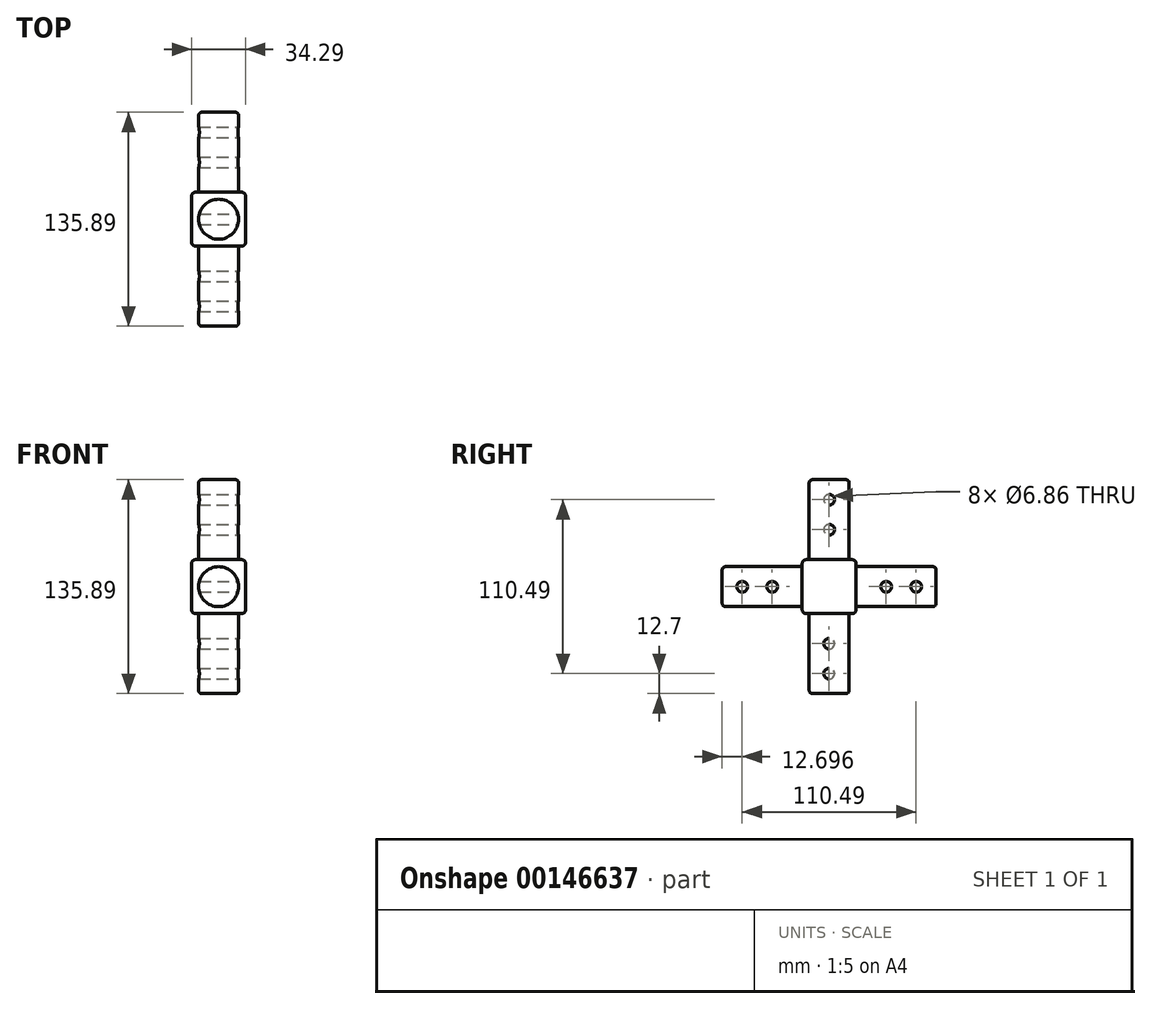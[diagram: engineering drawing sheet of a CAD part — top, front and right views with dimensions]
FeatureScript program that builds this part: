
annotation { "Feature Type Name" : "Feature", "Feature Type Description" : "" }
export const myFeature = defineFeature(function(context is Context, id is Id, definition is map)
    precondition{}
    {
        {
            var Q0;
            Q0=qCreatedBy(makeId("Top.planeOp"),FACE);
            var sketch = newSketch(context, id + "F0", { "sketchPlane" : qUnion([Q0])});
            skLineSegment(sketch, "E0.bottom", {"start": v(-13.47, 23.7) * mm, "end": v(20.82, 23.7) * mm});
            skLineSegment(sketch, "E0.top", {"start": v(-13.47, -10.58) * mm, "end": v(20.82, -10.58) * mm});
            skLineSegment(sketch, "E0.left", {"start": v(-13.47, 23.7) * mm, "end": v(-13.47, -10.58) * mm});
            skLineSegment(sketch, "E0.right", {"start": v(20.82, 23.7) * mm, "end": v(20.82, -10.58) * mm});
            skSolve(sketch);
        }
        {
            var Q0;
            Q0=qSketchRegion(id+"F0",true);
            extrude(context, id + "F1", {"entities" : qUnion([Q0]), "depth" : 34.3 * mm});
        }
        {
            var Q0;
            Q0=makeQuery(id+"F1.opExtrude","CAP_FACE",FACE,{"disambiguationData":[OSD([sQuery(id+"F0.wireOp",EDGE,"E0.bottom"),sQuery(id+"F0.wireOp",EDGE,"E0.top"),sQuery(id+"F0.wireOp",EDGE,"E0.left"),sQuery(id+"F0.wireOp",EDGE,"E0.right")])],"isStart":false});
            var sketch = newSketch(context, id + "F2", { "sketchPlane" : qUnion([Q0])});
            skCircle(sketch, "E1", {"center": v(3.68, 6.56) * mm, "radius": 12.7 * mm});
            skLineSegment(sketch, "E2", {"start": v(3.67, 23.7) * mm, "end": v(3.67, -12.79) * mm, "construction": true});
            skLineSegment(sketch, "E3", {"start": v(20.82, 6.56) * mm, "end": v(-13.47, 6.56) * mm, "construction": true});
            skSolve(sketch);
        }
        {
            var Q0;
            Q0=qSketchRegion(id+"F2",true);
            extrude(context, id + "F3", {"entities" : qUnion([Q0]), "operationType" : NewBodyOperationType.ADD, "depth" : 50.8 * mm});
        }
        {
            var Q0;
            Q0=makeQuery(id+"F1.opExtrude","SWEPT_FACE",FACE,{"disambiguationData":[OSD([sQuery(id+"F0.wireOp",EDGE,"E0.top")])]});
            var sketch = newSketch(context, id + "F4", { "sketchPlane" : qUnion([Q0])});
            skLineSegment(sketch, "E4", {"start": v(-13.47, 17.15) * mm, "end": v(24.43, 17.15) * mm, "construction": true});
            skLineSegment(sketch, "E5", {"start": v(3.67, 0) * mm, "end": v(3.67, 34.3) * mm, "construction": true});
            skCircle(sketch, "E6", {"center": v(3.67, 17.15) * mm, "radius": 12.7 * mm});
            skSolve(sketch);
        }
        {
            var Q0;
            Q0=qSketchRegion(id+"F4",true);
            extrude(context, id + "F5", {"entities" : qUnion([Q0]), "operationType" : NewBodyOperationType.ADD, "depth" : 50.8 * mm});
        }
        {
            var Q0;
            Q0=qCreatedBy(makeId("Right.planeOp"),FACE);
            var sketch = newSketch(context, id + "F6", { "sketchPlane" : qUnion([Q0])});
            skCircle(sketch, "E7", {"center": v(6.56, 53.34) * mm, "radius": 3.43 * mm});
            skCircle(sketch, "E8", {"center": v(6.56, 72.4) * mm, "radius": 3.43 * mm});
            skSolve(sketch);
        }
        {
            var Q0;
            Q0=qSketchRegion(id+"F6",true);
            extrude(context, id + "F7", {"entities" : qUnion([Q0]), "operationType" : NewBodyOperationType.REMOVE, "endBound" : BoundingType.SYMMETRIC, "oppositeDirection" : true, "depth" : 50.8 * mm});
        }
        {
            var Q0;
            Q0=qCreatedBy(makeId("Right.planeOp"),FACE);
            var sketch = newSketch(context, id + "F8", { "sketchPlane" : qUnion([Q0])});
            skCircle(sketch, "E9", {"center": v(-29.63, 17.15) * mm, "radius": 3.43 * mm});
            skCircle(sketch, "E10", {"center": v(-48.68, 17.15) * mm, "radius": 3.43 * mm});
            skSolve(sketch);
        }
        {
            var Q0;
            Q0=qSketchRegion(id+"F8",true);
            extrude(context, id + "F9", {"entities" : qUnion([Q0]), "operationType" : NewBodyOperationType.REMOVE, "endBound" : BoundingType.SYMMETRIC, "oppositeDirection" : true, "depth" : 50.8 * mm});
        }
        {
            var Q0;
            Q0=qCreatedBy(makeId("Front.planeOp"),FACE);
            var sketch = newSketch(context, id + "F10", { "sketchPlane" : qUnion([Q0])});
            skCircle(sketch, "E11", {"center": v(-51.57, 17.15) * mm, "radius": 3.43 * mm});
            skCircle(sketch, "E12", {"center": v(-32.52, 17.15) * mm, "radius": 3.43 * mm});
            skSolve(sketch);
        }
        {
            var Q0;
            Q0=qSketchRegion(id+"F10",true);
            extrude(context, id + "F11", {"entities" : qUnion([Q0]), "operationType" : NewBodyOperationType.REMOVE, "endBound" : BoundingType.SYMMETRIC, "oppositeDirection" : true, "depth" : 50.8 * mm});
        }
        {
            var Q0;
            Q0=makeQuery(id+"F1.opExtrude","SWEPT_EDGE",EDGE,{"disambiguationData":[OSD([sQuery(id+"F0.wireOp",EDGE,"E0.bottom"),sQuery(id+"F0.wireOp",EDGE,"E0.right")])]});
            var Q1;
            Q1=makeQuery(id+"F1.opExtrude","CAP_EDGE",EDGE,{"disambiguationData":[OSD([sQuery(id+"F0.wireOp",EDGE,"E0.right")])],"isStart":false});
            var Q2;
            Q2=makeQuery(id+"F1.opExtrude","SWEPT_EDGE",EDGE,{"disambiguationData":[OSD([sQuery(id+"F0.wireOp",EDGE,"E0.top"),sQuery(id+"F0.wireOp",EDGE,"E0.right")])]});
            var Q3;
            Q3=makeQuery(id+"F1.opExtrude","CAP_EDGE",EDGE,{"disambiguationData":[OSD([sQuery(id+"F0.wireOp",EDGE,"E0.right")])],"isStart":true});
            var Q4;
            Q4=makeQuery(id+"F1.opExtrude","CAP_EDGE",EDGE,{"disambiguationData":[OSD([sQuery(id+"F0.wireOp",EDGE,"E0.bottom")])],"isStart":true});
            var Q5;
            Q5=makeQuery(id+"F1.opExtrude","CAP_EDGE",EDGE,{"disambiguationData":[OSD([sQuery(id+"F0.wireOp",EDGE,"E0.bottom")])],"isStart":false});
            var Q6;
            Q6=makeQuery(id+"F1.opExtrude","SWEPT_EDGE",EDGE,{"disambiguationData":[OSD([sQuery(id+"F0.wireOp",EDGE,"E0.bottom"),sQuery(id+"F0.wireOp",EDGE,"E0.left")])]});
            var Q7;
            Q7=makeQuery(id+"F1.opExtrude","CAP_EDGE",EDGE,{"disambiguationData":[OSD([sQuery(id+"F0.wireOp",EDGE,"E0.left")])],"isStart":true});
            var Q8;
            Q8=makeQuery(id+"F1.opExtrude","CAP_EDGE",EDGE,{"disambiguationData":[OSD([sQuery(id+"F0.wireOp",EDGE,"E0.top")])],"isStart":true});
            var Q9;
            Q9=makeQuery(id+"F1.opExtrude","CAP_EDGE",EDGE,{"disambiguationData":[OSD([sQuery(id+"F0.wireOp",EDGE,"E0.left")])],"isStart":false});
            var Q10;
            Q10=makeQuery(id+"F1.opExtrude","SWEPT_EDGE",EDGE,{"disambiguationData":[OSD([sQuery(id+"F0.wireOp",EDGE,"E0.top"),sQuery(id+"F0.wireOp",EDGE,"E0.left")])]});
            var Q11;
            Q11=makeQuery(id+"F1.opExtrude","CAP_EDGE",EDGE,{"disambiguationData":[OSD([sQuery(id+"F0.wireOp",EDGE,"E0.top")])],"isStart":false});
            fillet(context, id + "F12", {"entities" : qUnion([Q0, Q1, Q2, Q3, Q4, Q5, Q6, Q7, Q8, Q9, Q10, Q11]), "radius" : 2.54 * mm, "tangentPropagation" : true, "allowEdgeOverflow" : false});
        }
        {
            var Q0;
            Q0=makeQuery(id+"F1.opExtrude","SWEPT_FACE",FACE,{"disambiguationData":[OSD([sQuery(id+"F0.wireOp",EDGE,"E0.bottom")])]});
            var sketch = newSketch(context, id + "F13", { "sketchPlane" : qUnion([Q0])});
            skLineSegment(sketch, "E13", {"start": v(-18.28, 17.15) * mm, "end": v(4.82, 17.15) * mm, "construction": true});
            skPoint(sketch, "E13.endSnap0", {"position": v(-18.28, 17.15) * mm});
            skLineSegment(sketch, "E14", {"start": v(-3.67, 31.75) * mm, "end": v(-3.67, 14.65) * mm, "construction": true});
            skCircle(sketch, "E15", {"center": v(-3.67, 17.15) * mm, "radius": 12.7 * mm});
            skSolve(sketch);
        }
        {
            var Q0;
            Q0=qSketchRegion(id+"F13",true);
            extrude(context, id + "F14", {"entities" : qUnion([Q0]), "operationType" : NewBodyOperationType.ADD, "depth" : 50.8 * mm});
        }
        {
            var Q0;
            Q0=qCreatedBy(makeId("Right.planeOp"),FACE);
            var sketch = newSketch(context, id + "F15", { "sketchPlane" : qUnion([Q0])});
            skCircle(sketch, "E16", {"center": v(42.76, 17.15) * mm, "radius": 3.43 * mm});
            skCircle(sketch, "E17", {"center": v(61.8, 17.15) * mm, "radius": 3.43 * mm});
            skSolve(sketch);
        }
        {
            var Q0;
            Q0=qSketchRegion(id+"F15",true);
            extrude(context, id + "F16", {"entities" : qUnion([Q0]), "operationType" : NewBodyOperationType.REMOVE, "endBound" : BoundingType.SYMMETRIC, "oppositeDirection" : true, "depth" : 50.8 * mm});
        }
        {
            var Q0;
            Q0=qCreatedBy(makeId("Front.planeOp"),FACE);
            var sketch = newSketch(context, id + "F17", { "sketchPlane" : qUnion([Q0])});
            skCircle(sketch, "E18", {"center": v(58.92, 17.15) * mm, "radius": 3.43 * mm});
            skCircle(sketch, "E19", {"center": v(39.87, 17.15) * mm, "radius": 3.43 * mm});
            skSolve(sketch);
        }
        {
            var Q0;
            Q0=qSketchRegion(id+"F17",true);
            extrude(context, id + "F18", {"entities" : qUnion([Q0]), "operationType" : NewBodyOperationType.REMOVE, "endBound" : BoundingType.SYMMETRIC, "oppositeDirection" : true, "depth" : 50.8 * mm});
        }
        {
            var Q0;
            Q0=makeQuery(id+"F1.opExtrude","CAP_FACE",FACE,{"disambiguationData":[OSD([sQuery(id+"F0.wireOp",EDGE,"E0.bottom"),sQuery(id+"F0.wireOp",EDGE,"E0.top"),sQuery(id+"F0.wireOp",EDGE,"E0.left"),sQuery(id+"F0.wireOp",EDGE,"E0.right")])],"isStart":true});
            var sketch = newSketch(context, id + "F19", { "sketchPlane" : qUnion([Q0])});
            skCircle(sketch, "E20", {"center": v(3.67, -6.56) * mm, "radius": 12.7 * mm});
            skPoint(sketch, "E20.centerSnap0", {"position": v(3.67, -21.17) * mm});
            skPoint(sketch, "E20.centerSnap1", {"position": v(-10.93, -6.56) * mm});
            skSolve(sketch);
        }
        {
            var Q0;
            Q0 = qSketchRegion(id + "F19", true);
            extrude(context, id + "F20", {"entities" : qUnion([Q0]), "operationType" : NewBodyOperationType.ADD, "depth" : 50.8 * mm});
        }
        {
            var Q0;
            Q0=qCreatedBy(makeId("Right.planeOp"),FACE);
            var sketch = newSketch(context, id + "F21", { "sketchPlane" : qUnion([Q0])});
            skCircle(sketch, "E21", {"center": v(6.56, -19.05) * mm, "radius": 3.43 * mm});
            skCircle(sketch, "E22", {"center": v(6.56, -38.1) * mm, "radius": 3.43 * mm});
            skSolve(sketch);
        }
        {
            var Q0;
            Q0 = qSketchRegion(id + "F21", true);
            extrude(context, id + "F22", {"entities" : qUnion([Q0]), "operationType" : NewBodyOperationType.REMOVE, "endBound" : BoundingType.SYMMETRIC, "oppositeDirection" : true, "depth" : 50.8 * mm});
        }
        {
            var Q0;
            Q0=makeQuery(id+"F3.opExtrude","CAP_EDGE",EDGE,{"disambiguationData":[OSD([sQuery(id+"F2.wireOp",EDGE,"E1")])],"isStart":false});
            var Q1;
            Q1=makeQuery(id+"F5.opExtrude","CAP_EDGE",EDGE,{"disambiguationData":[OSD([sQuery(id+"F4.wireOp",EDGE,"E6")])],"isStart":false});
            var Q2;
            Q2=makeQuery(id+"FYh3p2H8bsy1Prt_1.opExtrude","CAP_EDGE",EDGE,{"disambiguationData":[OSD([sQuery(id+"FIc3ZwD0MRkNizU_1.wireOp",EDGE,"5X2wenA0-NZPo-tNKO-rhVc-4ux0vwX6K1N9")])],"isStart":false});
            var Q3;
            Q3=makeQuery(id+"F14.opExtrude","CAP_EDGE",EDGE,{"disambiguationData":[OSD([sQuery(id+"F13.wireOp",EDGE,"E15")])],"isStart":false});
            var Q4;
            Q4=makeQuery(id+"F9gDW6ytOR0zG9s_1.opExtrude","CAP_EDGE",EDGE,{"disambiguationData":[OSD([sQuery(id+"FiyRrB6nUQmxvW3_1.wireOp",EDGE,"TDc28uEK-sT7R-I2aJ-wYcu-fXwbEVHNaGzo")])],"isStart":false});
            var Q5;
            Q5=makeQuery(id+"F20.opExtrude","CAP_EDGE",EDGE,{"disambiguationData":[OSD([sQuery(id+"F19.wireOp",EDGE,"E20")])],"isStart":false});
            fillet(context, id + "F23", {"entities" : qUnion([Q0, Q1, Q2, Q3, Q4, Q5]), "radius" : 2.03 * mm, "tangentPropagation" : true, "allowEdgeOverflow" : false});
        }
    });
